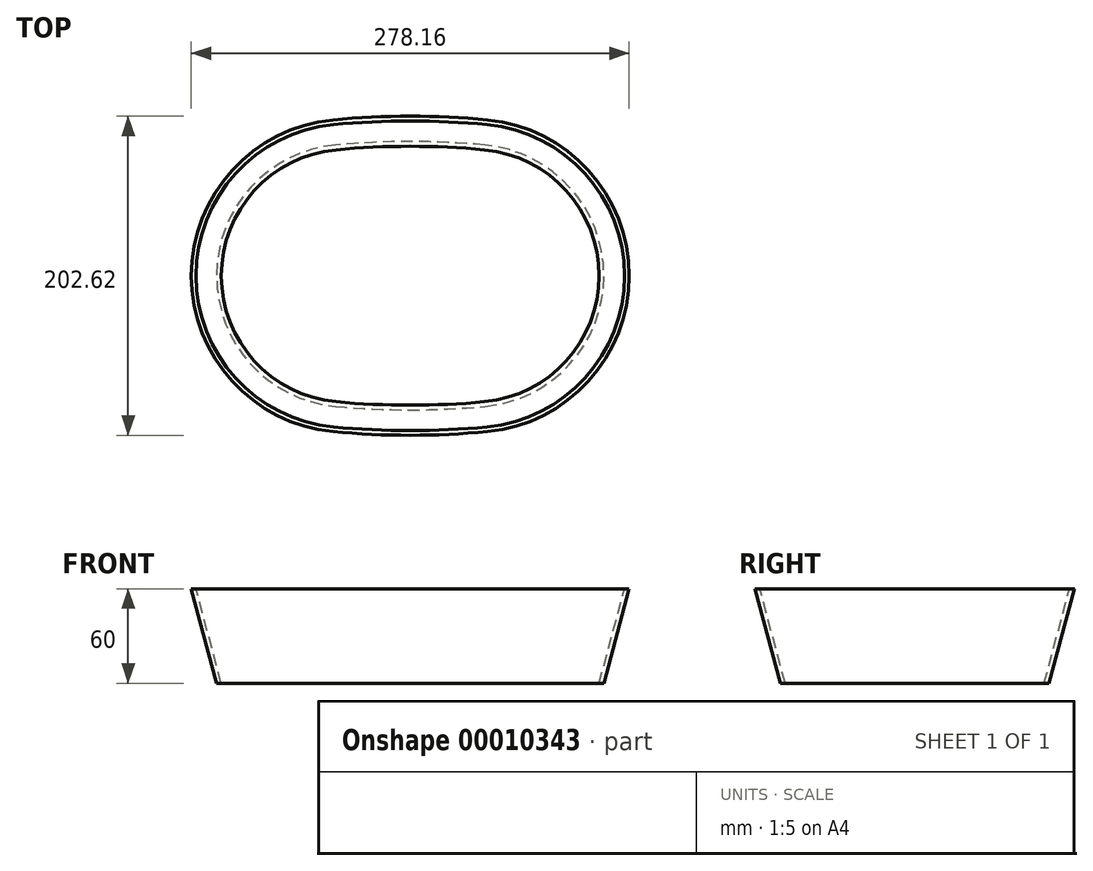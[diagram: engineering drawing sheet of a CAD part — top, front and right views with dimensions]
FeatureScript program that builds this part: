
annotation { "Feature Type Name" : "Feature", "Feature Type Description" : "" }
export const myFeature = defineFeature(function(context is Context, id is Id, definition is map)
    precondition{}
    {
        {
            var Q0;
            Q0=qCreatedBy(makeId("Top.planeOp"),FACE);
            var sketch = newSketch(context, id + "F0", { "sketchPlane" : qUnion([Q0])});
            skPoint(sketch, "E0.rect.middle", {"position": v(0, 0) * mm});
            skArc(sketch, "E1", {"start": v(-47.23, 80) * mm, "mid": v(-120, 0) * mm, "end": v(-47.23, -80) * mm});
            skLineSegment(sketch, "E2", {"start": v(0, 0) * mm, "end": v(-39.64, 0) * mm, "construction": true});
            skArc(sketch, "E3", {"start": v(47.23, 80) * mm, "mid": v(0, 82.24) * mm, "end": v(-47.23, 80) * mm});
            skLineSegment(sketch, "E4", {"start": v(0, -417.76) * mm, "end": v(0, 0) * mm, "construction": true});
            skLineSegment(sketch, "E5.rect.bottom", {"start": v(47.23, -80) * mm, "end": v(-47.23, -80) * mm, "construction": true});
            skLineSegment(sketch, "E5.rect.top", {"start": v(47.23, 80) * mm, "end": v(-47.23, 80) * mm, "construction": true});
            skArc(sketch, "E6", {"start": v(-47.23, -80) * mm, "mid": v(0, -82.24) * mm, "end": v(47.23, -80) * mm});
            skLineSegment(sketch, "E7", {"start": v(-120, 0) * mm, "end": v(120, 0) * mm, "construction": true});
            skArc(sketch, "E8", {"start": v(120, 0) * mm, "mid": v(99.09, 54.07) * mm, "end": v(47.23, 80) * mm});
            skArc(sketch, "E9", {"start": v(47.23, -80) * mm, "mid": v(99.09, -54.07) * mm, "end": v(120, 0) * mm});
            skSolve(sketch);
        }
        {
            var Q0;
            Q0=qCreatedBy(makeId("Front.planeOp"),FACE);
            var sketch = newSketch(context, id + "F1", { "sketchPlane" : qUnion([Q0])});
            skLineSegment(sketch, "E10", {"start": v(120, 0) * mm, "end": v(136.08, 60) * mm});
            skLineSegment(sketch, "E11", {"start": v(136.08, 60) * mm, "end": v(139.08, 60) * mm});
            skLineSegment(sketch, "E12", {"start": v(139.08, 60) * mm, "end": v(123, 0) * mm});
            skLineSegment(sketch, "E13", {"start": v(123, 0) * mm, "end": v(120, 0) * mm});
            skSolve(sketch);
        }
        {
            var Q0;
            Q0 = qSketchRegion(id + "F1", true);
            var Q1;
            Q1=sQuery(id+"F0.wireOp",EDGE,"E8");
            var Q2;
            Q2=sQuery(id+"F0.wireOp",EDGE,"E3");
            var Q3;
            Q3=sQuery(id+"F0.wireOp",EDGE,"E1");
            var Q4;
            Q4=sQuery(id+"F0.wireOp",EDGE,"E6");
            var Q5;
            Q5=sQuery(id+"F0.wireOp",EDGE,"E9");
            sweep(context, id + "F2", {"profiles" : qUnion([Q0]), "path" : qUnion([Q1, Q2, Q3, Q4, Q5])});
        }
    });
